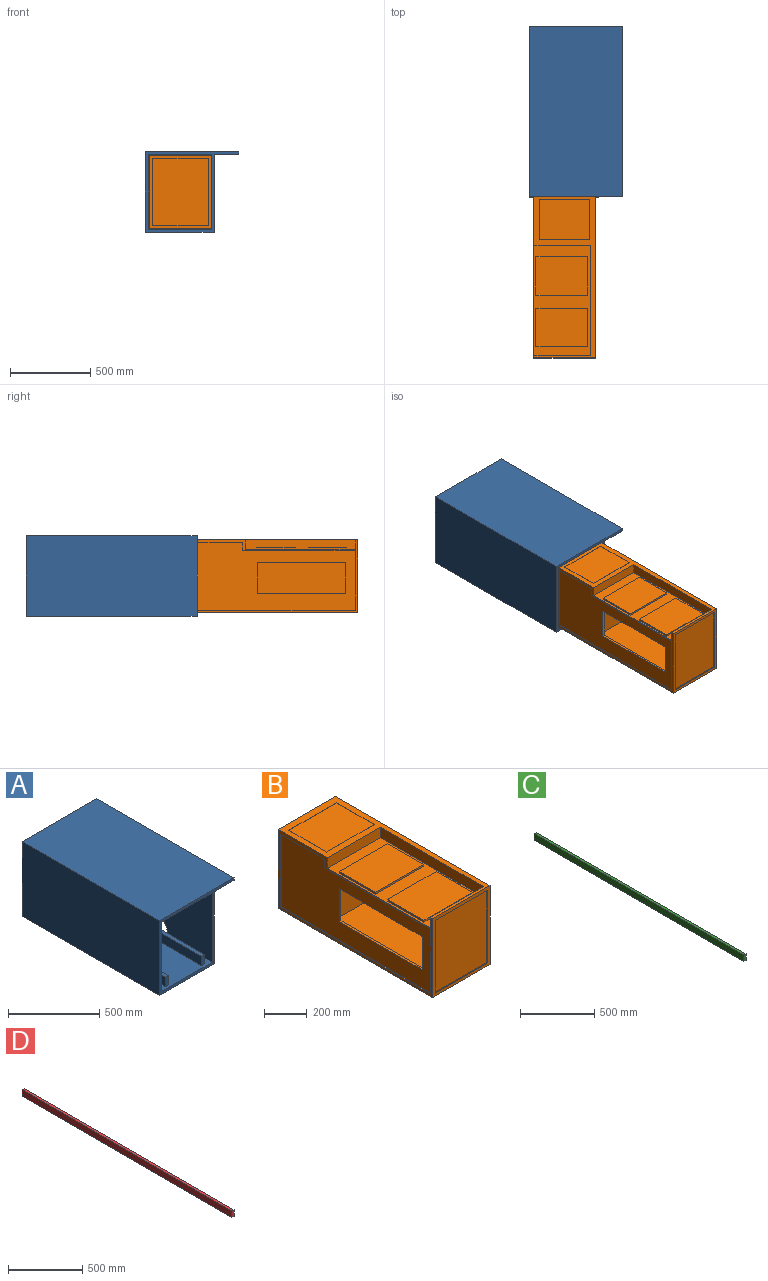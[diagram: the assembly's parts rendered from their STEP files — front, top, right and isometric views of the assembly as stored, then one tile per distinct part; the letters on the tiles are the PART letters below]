
ASSEMBLY  parts=4 mates=3
PART A: 23 faces, bbox 579x1062.5x500 mm
  f0: plane 1050x465mm, normal (-1,0,0), area 317641mm2, adj f2,f3,f8,f9,f19,f20
  f1: plane 1062.5x482.5mm, normal (1,0,0), area 342047.3mm2, adj f3,f6,f8,f10,f19,f20,f22
  f2: plane 1050x392mm, normal (0,0,-1), area 411600mm2, adj f0,f7,f8,f9
  f3: plane 1050x409.5mm, normal (0,0,1), area 372465.4mm2, adj f0,f1,f7,f8,f9,f11,f12,f14
  f4: plane 1062.5x579mm, normal (0,0,1), area 615187.5mm2, adj f5,f8,f10,f21
  f5: plane 1062.5x500mm, normal (-1,0,0), area 531250mm2, adj f4,f6,f8,f10
  f6: plane 1062.5x427mm, normal (0,0,-1), area 453687.5mm2, adj f1,f5,f8,f10
  f7: plane 1050x465mm, normal (1,0,0), area 488250mm2, adj f2,f3,f8,f9
  f8: plane 579x500mm, normal (0,-1,0), area 33880mm2, adj f0,f1,f2,f3,f4,f5,f6,f7
  f9: plane 465x392mm, normal (0,-1,0), area 179180mm2, adj f0,f2,f3,f7,f12,f13,f14,f16
  f10: plane 579x500mm, normal (0,1,0), area 216160mm2, adj f1,f4,f5,f6,f21,f22
  f11: plane 62x25mm, normal (0,-1,0), area 1550mm2, adj f3,f12,f13,f14
  f12: plane 1032.5x62mm, normal (-1,0,0), area 64015mm2, adj f3,f9,f11,f13
  f13: plane 1032.5x25mm, normal (0,0,1), area 25812.5mm2, adj f9,f11,f12,f14
  f14: plane 1032.5x62mm, normal (1,0,0), area 64015mm2, adj f3,f9,f11,f13
  f15: plane 62x25mm, normal (0,-1,0), area 1550mm2, adj f3,f16,f17,f18
  f16: plane 1032.5x62mm, normal (-1,0,0), area 64015mm2, adj f3,f9,f15,f17
  f17: plane 1032.5x25mm, normal (0,0,1), area 25812.5mm2, adj f9,f15,f16,f18
  f18: plane 1032.5x62mm, normal (1,0,0), area 64015mm2, adj f3,f9,f15,f17
  f19: plane 181.36x17.5mm, normal (0,-1,0), area 3173.7mm2, adj f0,f1,f3,f20
  f20: cylinder r=434.62mm len=713.74mm, axis (1,0,0), area 15374.1mm2, adj f0,f1,f3,f19
  f21: plane 1062.5x17.5mm, normal (1,0,0), area 18593.8mm2, adj f4,f8,f10,f22
  f22: plane 1062.5x152mm, normal (0,0,-1), area 161500mm2, adj f1,f8,f10,f21
PART B: 69 faces, bbox 380x1025x452.5 mm
  f0: plane 1025x380mm, normal (0,0,1), area 69853.5mm2, adj f1,f7,f10,f19,f22,f50,f57,f64
  f1: plane 452.5x380mm, normal (0,1,0), area 30434.4mm2, adj f0,f2,f6,f9,f14,f15,f16,f17
  f2: plane 1007.5x435mm, normal (1,0,0), area 438262.5mm2, adj f1,f20,f21,f51
  f3: plane 682.5x292.5mm, normal (1,0,0), area 95131.2mm2, adj f4,f18,f43,f44,f45,f46,f47,f59
  f4: plane 682.5x345mm, normal (0,0,-1), area 107590.5mm2, adj f3,f5,f33,f34,f35,f36,f38,f39
  f5: plane 682.5x292.5mm, normal (-1,0,0), area 199631.2mm2, adj f4,f18,f47,f59
  f6: plane 345x312.5mm, normal (0,0,1), area 107812.5mm2, adj f1,f9,f17,f58
  f7: plane 452.5x380mm, normal (0,-1,0), area 27912.5mm2, adj f0,f19,f20,f22,f52,f53,f54,f55
  f8: plane 990x420mm, normal (-1,0,0), area 277350mm2, adj f12,f13,f43,f44,f45,f46,f49,f60
  f9: plane 346.39x312.5mm, normal (1,0,0), area 108245.6mm2, adj f1,f6,f58,f63
  f10: plane 682.5x60mm, normal (-1,0,0), area 40950mm2, adj f0,f11,f50,f57
  f11: plane 682.5x352.5mm, normal (0,0,1), area 86981.3mm2, adj f10,f19,f23,f24,f25,f26,f28,f29
  f12: plane 700x5mm, normal (0,0,-1), area 3500mm2, adj f8,f19,f49,f62
  f13: plane 990x5mm, normal (0,0,1), area 4950mm2, adj f8,f19,f49,f60
  f14: plane 1007.5x57.5mm, normal (1,0,0), area 57931.3mm2, adj f1,f15,f20,f48
  f15: plane 1007.5x345mm, normal (0,0,-1), area 347587.5mm2, adj f1,f14,f16,f48
  f16: plane 1007.5x57.5mm, normal (-1,0,0), area 57931.3mm2, adj f1,f15,f20,f48
  f17: plane 346.39x312.5mm, normal (-1,0,0), area 108245.6mm2, adj f1,f6,f58,f63
  f18: plane 682.5x345mm, normal (0,0,1), area 235462.5mm2, adj f3,f5,f47,f59
  f19: plane 1025x452.5mm, normal (-1,0,0), area 41012.5mm2, adj f0,f1,f7,f11,f12,f13,f20,f49
  f20: plane 1025x380mm, normal (0,0,-1), area 36875mm2, adj f1,f2,f7,f14,f16,f19,f22,f48
  f21: plane 1007.5x5mm, normal (0,0,-1), area 5037.5mm2, adj f1,f2,f22,f51
  f22: plane 1025x452.5mm, normal (1,0,0), area 25550mm2, adj f0,f1,f7,f20,f21,f51
  f23: plane 240x10mm, normal (1,0,0), area 2400mm2, adj f11,f24,f26,f27
  f24: plane 320x10mm, normal (0,1,0), area 3200mm2, adj f11,f23,f25,f27
  f25: plane 240x10mm, normal (-1,0,0), area 2400mm2, adj f11,f24,f26,f27
  f26: plane 320x10mm, normal (0,-1,0), area 3200mm2, adj f11,f23,f25,f27
  f27: plane 320x240mm, normal (0,0,1), area 76800mm2, adj f23,f24,f25,f26
  f28: plane 240x10mm, normal (1,0,0), area 2400mm2, adj f11,f29,f31,f32
  f29: plane 320x10mm, normal (0,1,0), area 3200mm2, adj f11,f28,f30,f32
  f30: plane 240x10mm, normal (-1,0,0), area 2400mm2, adj f11,f29,f31,f32
  f31: plane 320x10mm, normal (0,-1,0), area 3200mm2, adj f11,f28,f30,f32
  f32: plane 320x240mm, normal (0,0,1), area 76800mm2, adj f28,f29,f30,f31
  f33: plane 216x30mm, normal (-1,0,0), area 6480mm2, adj f4,f34,f36,f37
  f34: plane 296x30mm, normal (0,-1,0), area 8880mm2, adj f4,f33,f35,f37
  f35: plane 216x30mm, normal (1,0,0), area 6480mm2, adj f4,f34,f36,f37
  f36: plane 296x30mm, normal (0,1,0), area 8880mm2, adj f4,f33,f35,f37
  f37: plane 296x216mm, normal (0,0,-1), area 63936mm2, adj f33,f34,f35,f36
  f38: plane 216x30mm, normal (-1,0,0), area 6480mm2, adj f4,f39,f41,f42
  f39: plane 296x30mm, normal (0,-1,0), area 8880mm2, adj f4,f38,f40,f42
  f40: plane 216x30mm, normal (1,0,0), area 6480mm2, adj f4,f39,f41,f42
  f41: plane 296x30mm, normal (0,1,0), area 8880mm2, adj f4,f38,f40,f42
  f42: plane 296x216mm, normal (0,0,-1), area 63936mm2, adj f38,f39,f40,f41
  f43: plane 190x12.5mm, normal (0,1,0), area 2375mm2, adj f3,f8,f44,f46
  f44: plane 550x12.5mm, normal (0,0,-1), area 6875mm2, adj f3,f8,f43,f45
  f45: plane 190x12.5mm, normal (0,-1,0), area 2375mm2, adj f3,f8,f44,f46
  f46: plane 550x12.5mm, normal (0,0,1), area 6875mm2, adj f3,f8,f43,f45
  f47: plane 345x292.5mm, normal (0,1,0), area 100912.5mm2, adj f3,f4,f5,f18
  f48: plane 345x57.5mm, normal (0,1,0), area 19837.5mm2, adj f14,f15,f16,f20
  f49: plane 371.5x5mm, normal (0,1,0), area 1857.5mm2, adj f8,f12,f13,f19
  f50: plane 352.5x60mm, normal (0,1,0), area 21150mm2, adj f0,f10,f11,f19
  f51: plane 435x5mm, normal (0,1,0), area 2175mm2, adj f2,f20,f21,f22
  f52: plane 345x5mm, normal (0,0,-1), area 1725mm2, adj f7,f53,f55,f56
  f53: plane 417.5x5mm, normal (1,0,0), area 2087.5mm2, adj f7,f52,f54,f56
  f54: plane 345x5mm, normal (0,0,1), area 1725mm2, adj f7,f53,f55,f56
  f55: plane 417.5x5mm, normal (-1,0,0), area 2087.5mm2, adj f7,f52,f54,f56
  f56: plane 417.5x345mm, normal (0,-1,0), area 144037.5mm2, adj f52,f53,f54,f55
  f57: plane 352.5x60mm, normal (0,-1,0), area 21150mm2, adj f0,f10,f11,f19
  f58: plane 346.39x345mm, normal (0,1,0), area 119503.1mm2, adj f6,f9,f17,f63
  f59: plane 345x292.5mm, normal (0,-1,0), area 100912.5mm2, adj f3,f4,f5,f18
  f60: plane 420x5mm, normal (0,-1,0), area 2100mm2, adj f8,f13,f19,f61
  f61: plane 290x5mm, normal (0,0,-1), area 1450mm2, adj f8,f19,f60,f62
  f62: plane 48.5x5mm, normal (0,1,0), area 242.5mm2, adj f8,f12,f19,f61
  f63: plane 345x312.5mm, normal (0,0,-1), area 107812.5mm2, adj f1,f9,f17,f58
  f64: plane 250x1mm, normal (1,0,0), area 250mm2, adj f0,f65,f67,f68
  f65: plane 316.26x1mm, normal (0,1,0), area 316.3mm2, adj f0,f64,f66,f68
  f66: plane 250x1mm, normal (-1,0,0), area 250mm2, adj f0,f65,f67,f68
  f67: plane 316.26x1mm, normal (0,-1,0), area 316.3mm2, adj f0,f64,f66,f68
  f68: plane 316.26x250mm, normal (0,0,1), area 79065.2mm2, adj f64,f65,f66,f67
PART C: 6 faces, bbox 19.5x2000x53 mm
  f0: plane 2000x19.5mm, normal (0,0,1), area 39000mm2, adj f1,f3,f4,f5
  f1: plane 2000x53mm, normal (-1,0,0), area 106000mm2, adj f0,f2,f4,f5
  f2: plane 2000x19.5mm, normal (0,0,-1), area 39000mm2, adj f1,f3,f4,f5
  f3: plane 2000x53mm, normal (1,0,0), area 106000mm2, adj f0,f2,f4,f5
  f4: plane 53x19.5mm, normal (0,-1,0), area 1033.5mm2, adj f0,f1,f2,f3
  f5: plane 53x19.5mm, normal (0,1,0), area 1033.5mm2, adj f0,f1,f2,f3
PART D: 6 faces, bbox 19.5x2000x53 mm
  f0: plane 2000x19.5mm, normal (0,0,1), area 39000mm2, adj f1,f3,f4,f5
  f1: plane 2000x53mm, normal (-1,0,0), area 106000mm2, adj f0,f2,f4,f5
  f2: plane 2000x19.5mm, normal (0,0,-1), area 39000mm2, adj f1,f3,f4,f5
  f3: plane 2000x53mm, normal (1,0,0), area 106000mm2, adj f0,f2,f4,f5
  f4: plane 53x19.5mm, normal (0,-1,0), area 1033.5mm2, adj f0,f1,f2,f3
  f5: plane 53x19.5mm, normal (0,1,0), area 1033.5mm2, adj f0,f1,f2,f3
PLACE A t=(-84.35,1104.92,-5.56)mm
PLACE B t=(105.7,104.92,231.19)mm
PLACE C t=(269.35,2122.42,110.25)mm
PLACE D t=(269.35,2122.42,110.25)mm
MATE fastened C.f3 <-> A.f12  axis (1,0,0) through (-36.65,1122.42,30.44)mm
MATE fastened B.f48 <-> D.f4  axis (0,-1,0) through (288.85,122.42,56.94)mm
MATE fastened C.f4 <-> B.f48  axis (0,1,0) through (-56.15,122.42,56.94)mm
